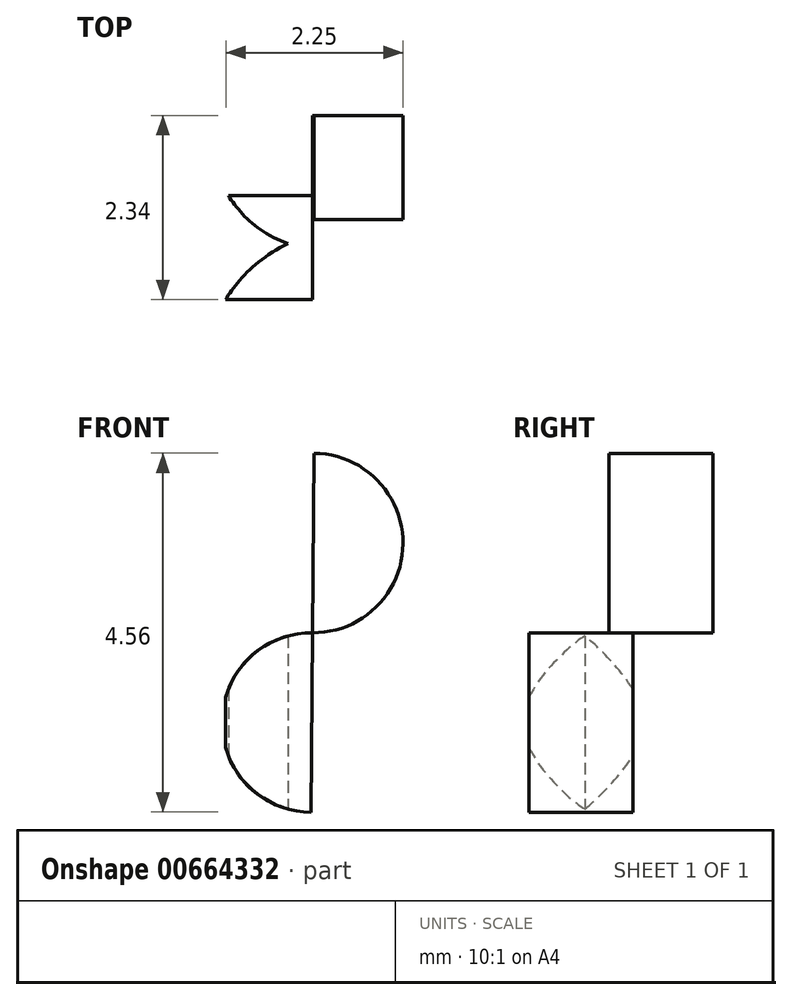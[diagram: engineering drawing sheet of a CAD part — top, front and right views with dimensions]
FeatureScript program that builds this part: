
annotation { "Feature Type Name" : "Feature", "Feature Type Description" : "" }
export const myFeature = defineFeature(function(context is Context, id is Id, definition is map)
    precondition{}
    {
        {
            var Q0;
            Q0=qCreatedBy(makeId("Front.planeOp"),FACE);
            var sketch = newSketch(context, id + "F0", { "sketchPlane" : qUnion([Q0])});
            skArc(sketch, "E0", {"start": v(-32.16, 50.32) * mm, "mid": v(-31, 51.45) * mm, "end": v(-32.14, 52.6) * mm});
            skLineSegment(sketch, "E1", {"start": v(-32.14, 52.6) * mm, "end": v(-32.16, 50.32) * mm});
            skSolve(sketch);
        }
        {
            var Q0;
            Q0=makeQuery(id+"F0.imprint","IMPRINT",FACE,{"disambiguationData":[TD([[makeQuery(id+"F0.imprint","IMPRINT",EDGE,{"derivedFrom":sQuery(id+"F0.wireOp",EDGE,"E0")}),1.0]])]});
            extrude(context, id + "F1", {"entities" : qUnion([Q0]), "depth" : 1.32 * mm, "offsetDistance" : 25.4 * mm});
        }
        {
            var Q0;
            Q0=makeQuery(id+"F1.opExtrude","SWEPT_BODY",BODY,{"disambiguationData":[OSD([sQuery(id+"F0.wireOp",EDGE,"E0"),sQuery(id+"F0.wireOp",EDGE,"E1")])]});
            var Q1;
            {var subQ0=sQuery(id+"F0.wireOp",EDGE,"E1");var subQ1=sQuery(id+"F0.wireOp",EDGE,"E0");Q1=makeQuery(id+"F1.opExtrude","SWEPT_EDGE",EDGE,{"disambiguationData":[OSD([subQ1,subQ0]),TDD([makeQuery(id+"F0.imprint","INTERSECT",VERTEX,{"disambiguationData":[OD(0.0)],"derivedFrom":[subQ1,subQ0]})])]});}
            transform(context, id + "F2", {"entities" : qUnion([Q0]), "transformType" : TransformType.ROTATION, "transformAxis" : qUnion([Q1]), "angle" : 180 * degree, "makeCopy" : true});
        }
        {
            var Q0;
            Q0=makeQuery(id+"F2.opPattern","COPY",BODY,{"derivedFrom":makeQuery(id+"F1.opExtrude","SWEPT_BODY",BODY,{"disambiguationData":[OSD([sQuery(id+"F0.wireOp",EDGE,"E0"),sQuery(id+"F0.wireOp",EDGE,"E1")])]}),"instanceName":"1"});
            transform(context, id + "F3", {"entities" : qUnion([Q0]), "transformType" : TransformType.TRANSLATION_3D, "dx" : 0 * mm, "dy" : -1.02 * mm, "dz" : 0 * mm, "makeCopy" : false});
        }
        {
            var Q0;
            Q0=qCreatedBy(makeId("Top.planeOp"),FACE);
            var sketch = newSketch(context, id + "F4", { "sketchPlane" : qUnion([Q0])});
            skArc(sketch, "E2", {"start": v(-33.35, -0.75) * mm, "mid": v(-33.01, -1.3) * mm, "end": v(-32.47, -1.63) * mm});
            skArc(sketch, "E3", {"start": v(-32.47, -1.63) * mm, "mid": v(-32.98, -1.99) * mm, "end": v(-33.35, -2.5) * mm});
            skLineSegment(sketch, "E4", {"start": v(-33.35, -2.5) * mm, "end": v(-33.35, -0.75) * mm});
            skSolve(sketch);
        }
        {
            var Q0;
            Q0=makeQuery(id+"F4.imprint","IMPRINT",FACE,{"disambiguationData":[TD([[makeQuery(id+"F4.imprint","IMPRINT",EDGE,{"derivedFrom":sQuery(id+"F4.wireOp",EDGE,"E2")}),-1.0]])]});
            extrude(context, id + "F5", {"entities" : qUnion([Q0]), "operationType" : NewBodyOperationType.REMOVE, "depth" : 101.6 * mm, "offsetDistance" : 25.4 * mm});
        }
    });
